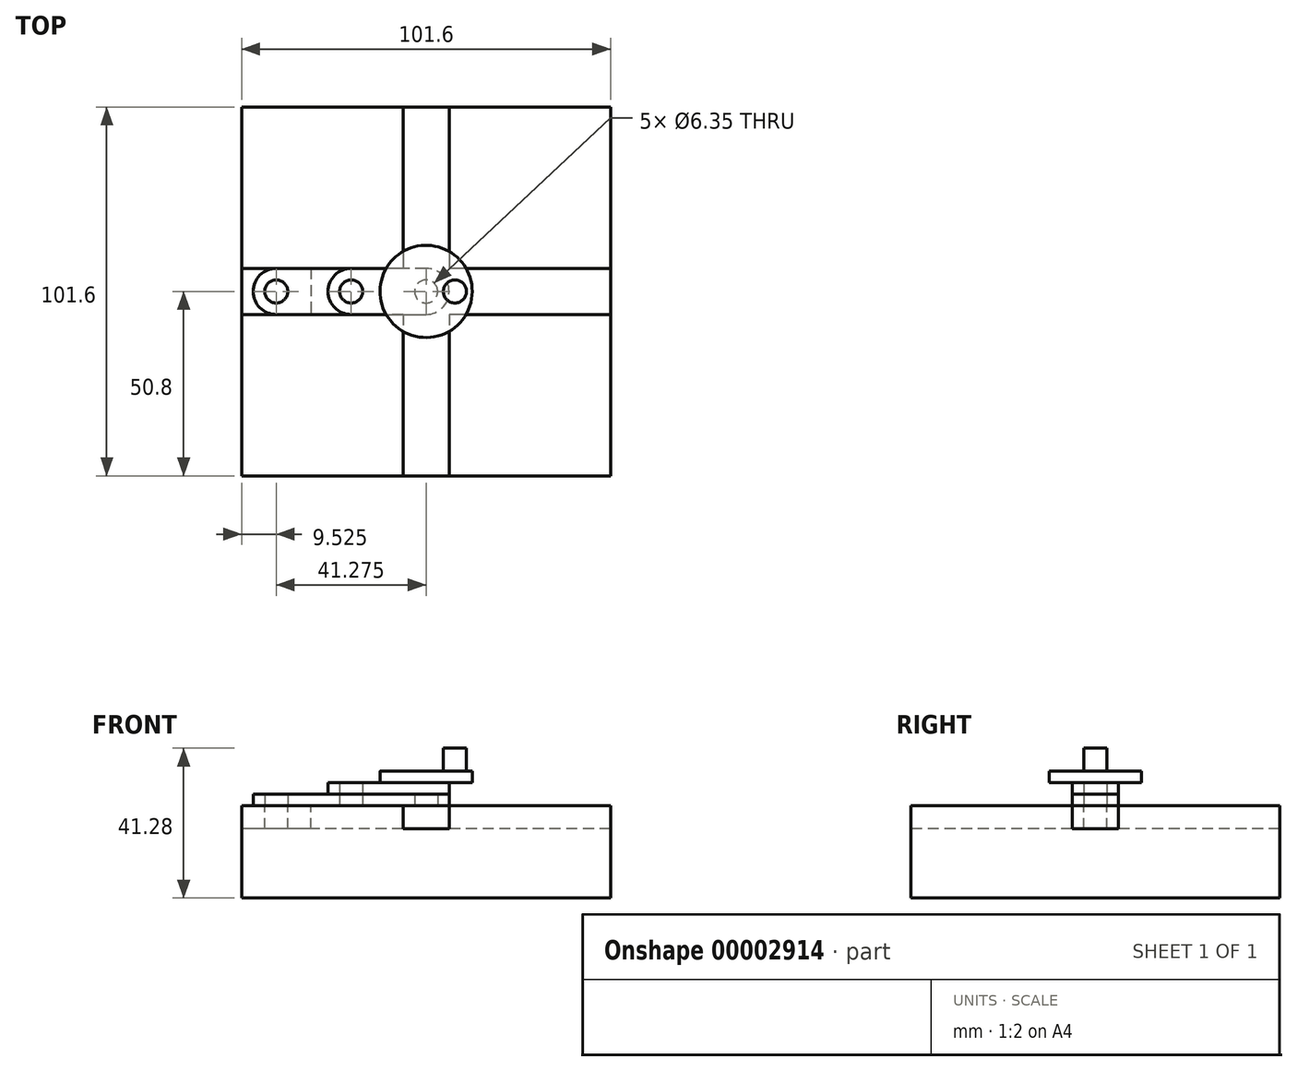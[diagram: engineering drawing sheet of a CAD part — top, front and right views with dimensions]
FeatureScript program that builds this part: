
annotation { "Feature Type Name" : "Feature", "Feature Type Description" : "" }
export const myFeature = defineFeature(function(context is Context, id is Id, definition is map)
    precondition{}
    {
        {
            var Q0;
            Q0=qCreatedBy(makeId("Top.planeOp"),FACE);
            var sketch = newSketch(context, id + "F0", { "sketchPlane" : qUnion([Q0])});
            skLineSegment(sketch, "E0.rect.bottom", {"start": v(50.8, 50.8) * mm, "end": v(-50.8, 50.8) * mm});
            skLineSegment(sketch, "E0.rect.top", {"start": v(50.8, -50.8) * mm, "end": v(-50.8, -50.8) * mm});
            skLineSegment(sketch, "E0.rect.left", {"start": v(50.8, 50.8) * mm, "end": v(50.8, -50.8) * mm});
            skLineSegment(sketch, "E0.rect.right", {"start": v(-50.8, 50.8) * mm, "end": v(-50.8, -50.8) * mm});
            skPoint(sketch, "E0.rect.middle", {"position": v(0, 0) * mm});
            skSolve(sketch);
        }
        {
            var Q0;
            Q0=makeQuery(id+"F0.imprint","IMPRINT",FACE,{"disambiguationData":[TD([[makeQuery(id+"F0.imprint","IMPRINT",EDGE,{"derivedFrom":sQuery(id+"F0.wireOp",EDGE,"E0.rect.bottom")}),1.0]])]});
            extrude(context, id + "F1", {"entities" : qUnion([Q0]), "depth" : 25.4 * mm});
        }
        {
            var Q0;
            Q0=makeQuery(id+"F1.opExtrude","CAP_FACE",FACE,{"disambiguationData":[OSD([sQuery(id+"F0.wireOp",EDGE,"E0.rect.bottom"),sQuery(id+"F0.wireOp",EDGE,"E0.rect.top"),sQuery(id+"F0.wireOp",EDGE,"E0.rect.left"),sQuery(id+"F0.wireOp",EDGE,"E0.rect.right")])],"isStart":false});
            var sketch = newSketch(context, id + "F2", { "sketchPlane" : qUnion([Q0])});
            skLineSegment(sketch, "E1.rect.bottom", {"start": v(50.8, -6.35) * mm, "end": v(-50.8, -6.35) * mm});
            skLineSegment(sketch, "E1.rect.top", {"start": v(50.8, 6.35) * mm, "end": v(-50.8, 6.35) * mm});
            skLineSegment(sketch, "E1.rect.left", {"start": v(50.8, -6.35) * mm, "end": v(50.8, 6.35) * mm});
            skLineSegment(sketch, "E1.rect.right", {"start": v(-50.8, -6.35) * mm, "end": v(-50.8, 6.35) * mm});
            skPoint(sketch, "E1.rect.middle", {"position": v(0, 0) * mm});
            skLineSegment(sketch, "E2.rect.bottom", {"start": v(6.35, 50.8) * mm, "end": v(-6.35, 50.8) * mm});
            skLineSegment(sketch, "E2.rect.top", {"start": v(6.35, -50.8) * mm, "end": v(-6.35, -50.8) * mm});
            skLineSegment(sketch, "E2.rect.left", {"start": v(6.35, 50.8) * mm, "end": v(6.35, -50.8) * mm});
            skLineSegment(sketch, "E2.rect.right", {"start": v(-6.35, 50.8) * mm, "end": v(-6.35, -50.8) * mm});
            skLineSegment(sketch, "E3", {"start": v(-31.75, 6.35) * mm, "end": v(-31.75, -6.35) * mm});
            skSolve(sketch);
        }
        {
            var Q0;
            {var subQ0=sQuery(id+"F2.wireOp",EDGE,"E2.rect.left");var subQ3=sQuery(id+"F2.wireOp",EDGE,"E1.rect.bottom");var subQ4=makeQuery(id+"F2.imprint","INTERSECT",VERTEX,{"derivedFrom":[subQ3,subQ0]});var subQ6=sQuery(id+"F2.wireOp",EDGE,"E1.rect.left");var subQ11=sQuery(id+"F2.wireOp",EDGE,"E2.rect.top");var subQ12=makeQuery(id+"F2.imprint","IMPRINT",EDGE,{"disambiguationData":[TD([[subQ4,-1.0]])],"derivedFrom":subQ3});var subQ13=sQuery(id+"F2.wireOp",EDGE,"E3");var subQ14=makeQuery(id+"F2.imprint","IMPRINT",EDGE,{"derivedFrom":subQ13});var subQ15=sQuery(id+"F2.wireOp",EDGE,"E1.rect.right");var subQ21=sQuery(id+"F2.wireOp",EDGE,"E2.rect.bottom");Q0=qUnion([makeQuery(id+"F2.imprint","IMPRINT",FACE,{"disambiguationData":[TD([[makeQuery(id+"F2.imprint","IMPRINT",EDGE,{"derivedFrom":subQ6}),-1.0]])]}),makeQuery(id+"F2.imprint","IMPRINT",FACE,{"disambiguationData":[TD([[makeQuery(id+"F2.imprint","IMPRINT",EDGE,{"derivedFrom":subQ11}),-1.0]])]}),makeQuery(id+"F2.imprint","IMPRINT",FACE,{"disambiguationData":[TD([[makeQuery(id+"F2.imprint","IMPRINT",EDGE,{"derivedFrom":subQ15}),1.0]])]}),makeQuery(id+"F2.imprint","IMPRINT",FACE,{"disambiguationData":[TD([[makeQuery(id+"F2.imprint","IMPRINT",EDGE,{"derivedFrom":subQ21}),1.0]])]}),makeQuery(id+"F2.imprint","IMPRINT",FACE,{"disambiguationData":[TD([[subQ12,-1.0]])]}),makeQuery(id+"F2.imprint","IMPRINT",FACE,{"disambiguationData":[TD([[subQ14,1.0]])]})]);}
            extrude(context, id + "F3", {"entities" : qUnion([Q0]), "operationType" : NewBodyOperationType.REMOVE, "oppositeDirection" : true, "depth" : 6.35 * mm});
        }
        {
            var Q0;
            {var subQ1=sQuery(id+"F2.wireOp",EDGE,"E1.rect.right");Q0=makeQuery(id+"F2.imprint","IMPRINT",FACE,{"disambiguationData":[TD([[makeQuery(id+"F2.imprint","IMPRINT",EDGE,{"derivedFrom":subQ1}),1.0]])]});}
            extrude(context, id + "F4", {"entities" : qUnion([Q0]), "oppositeDirection" : true, "depth" : 6.35 * mm});
        }
        {
            var Q0;
            {var subQ1=sQuery(id+"F2.wireOp",EDGE,"E1.rect.right");Q0=makeQuery(id+"F2.imprint","IMPRINT",FACE,{"disambiguationData":[TD([[makeQuery(id+"F2.imprint","IMPRINT",EDGE,{"derivedFrom":subQ1}),1.0]])]});}
            var sketch = newSketch(context, id + "F5", { "sketchPlane" : qUnion([Q0])});
            skPoint(sketch, "E4.0", {"position": v(-31.75, 6.35) * mm});
            skPoint(sketch, "E5.0", {"position": v(-50.8, -6.35) * mm});
            skLineSegment(sketch, "E6", {"start": v(-50.8, -6.35) * mm, "end": v(-31.75, 6.35) * mm, "construction": true});
            skCircle(sketch, "E7", {"center": v(-41.27, 0) * mm, "radius": 3.18 * mm});
            skSolve(sketch);
        }
        {
            var Q0;
            Q0=makeQuery(id+"F5.imprint","IMPRINT",FACE,{"disambiguationData":[TD([[makeQuery(id+"F5.imprint","IMPRINT",EDGE,{"derivedFrom":sQuery(id+"F5.wireOp",EDGE,"E7")}),1.0]])]});
            var Q1;
            Q1=makeQuery(id+"F4.opExtrude","CAP_FACE",FACE,{"disambiguationData":[OSD([sQuery(id+"F2.wireOp",EDGE,"E1.rect.bottom"),sQuery(id+"F2.wireOp",EDGE,"E1.rect.top"),sQuery(id+"F2.wireOp",EDGE,"E1.rect.right"),sQuery(id+"F2.wireOp",EDGE,"E3")])],"isStart":false});
            extrude(context, id + "F6", {"entities" : qUnion([Q0]), "operationType" : NewBodyOperationType.REMOVE, "endBound" : BoundingType.UP_TO_SURFACE, "oppositeDirection" : true, "endBoundEntityFace" : qUnion([Q1]), "depth" : 25.4 * mm});
        }
        {
            var Q0;
            {var subQ0=sQuery(id+"F0.wireOp",EDGE,"E0.rect.bottom");var subQ1=sQuery(id+"F0.wireOp",EDGE,"E0.rect.right");var subQ2=sQuery(id+"F2.wireOp",EDGE,"E2.rect.right");var subQ3=sQuery(id+"F2.wireOp",EDGE,"E1.rect.top");var subQ4=makeQuery(id+"F2.imprint","INTERSECT",VERTEX,{"derivedFrom":[subQ3,subQ2]});Q0=makeQuery(id+"F3.boolean.opBoolean","SPLIT",FACE,{"disambiguationData":[TD([makeQuery(id+"F3.opExtrude","SWEPT_FACE",FACE,{"disambiguationData":[OSD([subQ2]),TDD([makeQuery(id+"F2.imprint","IMPRINT",EDGE,{"disambiguationData":[TD([[subQ4,1.0]])],"derivedFrom":subQ2})])]})])],"derivedFrom":makeQuery(id+"F1.opExtrude","CAP_FACE",FACE,{"disambiguationData":[OSD([subQ0,sQuery(id+"F0.wireOp",EDGE,"E0.rect.top"),sQuery(id+"F0.wireOp",EDGE,"E0.rect.left"),subQ1])],"isStart":false})});}
            var sketch = newSketch(context, id + "F7", { "sketchPlane" : qUnion([Q0])});
            skPoint(sketch, "E8.0", {"position": v(0, 0) * mm});
            skCircle(sketch, "E9.0", {"center": v(-41.27, 0) * mm, "radius": 3.18 * mm});
            skCircle(sketch, "E10", {"center": v(0, 0) * mm, "radius": 3.18 * mm});
            skCircle(sketch, "E11.0", {"center": v(-41.27, 0) * mm, "radius": 6.35 * mm});
            skCircle(sketch, "E12.0", {"center": v(0, 0) * mm, "radius": 6.35 * mm});
            skLineSegment(sketch, "E13", {"start": v(-41.27, 6.35) * mm, "end": v(0, 6.35) * mm});
            skLineSegment(sketch, "E14", {"start": v(-41.27, -6.35) * mm, "end": v(0, -6.35) * mm});
            skLineSegment(sketch, "E15", {"start": v(-41.27, 0) * mm, "end": v(0, 0) * mm, "construction": true});
            skCircle(sketch, "E16", {"center": v(-20.64, 0) * mm, "radius": 3.18 * mm});
            skCircle(sketch, "E17", {"center": v(-20.64, 0) * mm, "radius": 6.35 * mm});
            skSolve(sketch);
        }
        {
            var Q0;
            {var subQ0=sQuery(id+"F7.wireOp",EDGE,"E11.0");var subQ1=sQuery(id+"F7.wireOp",EDGE,"E14");var subQ2=makeQuery(id+"F7.imprint","INTERSECT",VERTEX,{"derivedFrom":[subQ0,subQ1]});var subQ10=sQuery(id+"F7.wireOp",EDGE,"E12.0");var subQ12=makeQuery(id+"F7.imprint","INTERSECT",VERTEX,{"derivedFrom":[subQ10,subQ1]});var subQ13=makeQuery(id+"F7.imprint","IMPRINT",EDGE,{"disambiguationData":[TD([[subQ12,1.0]])],"derivedFrom":subQ10});Q0=qUnion([makeQuery(id+"F7.imprint","IMPRINT",FACE,{"disambiguationData":[TD([[makeQuery(id+"F7.imprint","IMPRINT",EDGE,{"derivedFrom":sQuery(id+"F7.wireOp",EDGE,"E9.0")}),-1.0]])]}),makeQuery(id+"F7.imprint","IMPRINT",FACE,{"disambiguationData":[TD([[makeQuery(id+"F7.imprint","IMPRINT",EDGE,{"derivedFrom":sQuery(id+"F7.wireOp",EDGE,"E10")}),-1.0]])]}),makeQuery(id+"F7.imprint","IMPRINT",FACE,{"disambiguationData":[TD([[makeQuery(id+"F7.imprint","IMPRINT",EDGE,{"disambiguationData":[TD([[subQ2,-1.0]])],"derivedFrom":subQ1}),1.0]])]}),makeQuery(id+"F7.imprint","IMPRINT",FACE,{"disambiguationData":[TD([[subQ13,-1.0]])]}),makeQuery(id+"F7.imprint","IMPRINT",FACE,{"disambiguationData":[TD([[makeQuery(id+"F7.imprint","IMPRINT",EDGE,{"derivedFrom":sQuery(id+"F7.wireOp",EDGE,"E16")}),-1.0]])]})]);}
            extrude(context, id + "F8", {"entities" : qUnion([Q0]), "depth" : 3.17 * mm});
        }
        {
            var Q0;
            Q0=makeQuery(id+"F8.opExtrude","CAP_FACE",FACE,{"disambiguationData":[OSD([sQuery(id+"F7.wireOp",EDGE,"E9.0"),sQuery(id+"F7.wireOp",EDGE,"E10"),sQuery(id+"F7.wireOp",EDGE,"E11.0"),sQuery(id+"F7.wireOp",EDGE,"E12.0"),sQuery(id+"F7.wireOp",EDGE,"E13"),sQuery(id+"F7.wireOp",EDGE,"E14"),sQuery(id+"F7.wireOp",EDGE,"E16")])],"isStart":false});
            var sketch = newSketch(context, id + "F9", { "sketchPlane" : qUnion([Q0])});
            skCircle(sketch, "E18.0", {"center": v(-20.64, 0) * mm, "radius": 6.35 * mm});
            skCircle(sketch, "E18.1", {"center": v(0, 0) * mm, "radius": 6.35 * mm});
            skCircle(sketch, "E18.2", {"center": v(0, 0) * mm, "radius": 3.18 * mm});
            skCircle(sketch, "E18.3", {"center": v(-20.64, 0) * mm, "radius": 3.18 * mm});
            skLineSegment(sketch, "E19", {"start": v(-20.64, 6.35) * mm, "end": v(0, 6.35) * mm});
            skLineSegment(sketch, "E20", {"start": v(0, -6.35) * mm, "end": v(-20.64, -6.35) * mm});
            skSolve(sketch);
        }
        {
            var Q0;
            {var subQ1=sQuery(id+"F9.wireOp",EDGE,"E19");Q0=qUnion([makeQuery(id+"F9.imprint","IMPRINT",FACE,{"disambiguationData":[TD([[makeQuery(id+"F9.imprint","IMPRINT",EDGE,{"derivedFrom":subQ1}),1.0]])]}),makeQuery(id+"F9.imprint","IMPRINT",FACE,{"disambiguationData":[TD([[makeQuery(id+"F9.imprint","IMPRINT",EDGE,{"derivedFrom":sQuery(id+"F9.wireOp",EDGE,"E18.2")}),-1.0]])]}),makeQuery(id+"F9.imprint","IMPRINT",FACE,{"disambiguationData":[TD([[makeQuery(id+"F9.imprint","IMPRINT",EDGE,{"derivedFrom":sQuery(id+"F9.wireOp",EDGE,"E18.3")}),-1.0]])]})]);}
            extrude(context, id + "F10", {"entities" : qUnion([Q0]), "depth" : 3.17 * mm});
        }
        {
            var Q0;
            Q0=makeQuery(id+"F8.opExtrude","CAP_FACE",FACE,{"disambiguationData":[OSD([sQuery(id+"F7.wireOp",EDGE,"E9.0"),sQuery(id+"F7.wireOp",EDGE,"E10"),sQuery(id+"F7.wireOp",EDGE,"E11.0"),sQuery(id+"F7.wireOp",EDGE,"E12.0"),sQuery(id+"F7.wireOp",EDGE,"E13"),sQuery(id+"F7.wireOp",EDGE,"E14"),sQuery(id+"F7.wireOp",EDGE,"E16")])],"isStart":false});
            var sketch = newSketch(context, id + "F11", { "sketchPlane" : qUnion([Q0])});
            skCircle(sketch, "E21.0", {"center": v(0, 0) * mm, "radius": 3.18 * mm});
            skSolve(sketch);
        }
        {
            var Q0;
            Q0=makeQuery(id+"F11.imprint","IMPRINT",FACE,{"disambiguationData":[TD([[makeQuery(id+"F11.imprint","IMPRINT",EDGE,{"derivedFrom":sQuery(id+"F11.wireOp",EDGE,"E21.0")}),1.0]])]});
            extrude(context, id + "F12", {"entities" : qUnion([Q0]), "depth" : 3.17 * mm});
        }
        {
            var Q0;
            Q0=makeQuery(id+"F12.opExtrude","CAP_FACE",FACE,{"disambiguationData":[OSD([sQuery(id+"F11.wireOp",EDGE,"E21.0")])],"isStart":false});
            var sketch = newSketch(context, id + "F13", { "sketchPlane" : qUnion([Q0])});
            skCircle(sketch, "E22.0", {"center": v(0, 0) * mm, "radius": 3.18 * mm});
            skCircle(sketch, "E23", {"center": v(0, 0) * mm, "radius": 12.7 * mm});
            skSolve(sketch);
        }
        {
            var Q0;
            Q0=makeQuery(id+"F13.imprint","IMPRINT",FACE,{"disambiguationData":[TD([[makeQuery(id+"F13.imprint","IMPRINT",EDGE,{"derivedFrom":sQuery(id+"F13.wireOp",EDGE,"E22.0")}),-1.0]])]});
            var Q1;
            Q1=makeQuery(id+"F13.imprint","IMPRINT",FACE,{"disambiguationData":[TD([[makeQuery(id+"F13.imprint","IMPRINT",EDGE,{"derivedFrom":sQuery(id+"F13.wireOp",EDGE,"E22.0")}),1.0]])]});
            extrude(context, id + "F14", {"entities" : qUnion([Q0, Q1]), "operationType" : NewBodyOperationType.ADD, "depth" : 3.17 * mm});
        }
        {
            var Q0;
            Q0=makeQuery(id+"F14.opExtrude","CAP_FACE",FACE,{"disambiguationData":[OSD([sQuery(id+"F13.wireOp",EDGE,"E23")])],"isStart":false});
            var sketch = newSketch(context, id + "F15", { "sketchPlane" : qUnion([Q0])});
            skCircle(sketch, "E24.0", {"center": v(0, 0) * mm, "radius": 12.7 * mm});
            skCircle(sketch, "E25", {"center": v(7.94, 0) * mm, "radius": 3.18 * mm});
            skSolve(sketch);
        }
        {
            var Q0;
            Q0=makeQuery(id+"F15.imprint","IMPRINT",FACE,{"disambiguationData":[TD([[makeQuery(id+"F15.imprint","IMPRINT",EDGE,{"derivedFrom":sQuery(id+"F15.wireOp",EDGE,"E25")}),1.0]])]});
            extrude(context, id + "F16", {"entities" : qUnion([Q0]), "operationType" : NewBodyOperationType.ADD, "depth" : 6.35 * mm});
        }
    });
